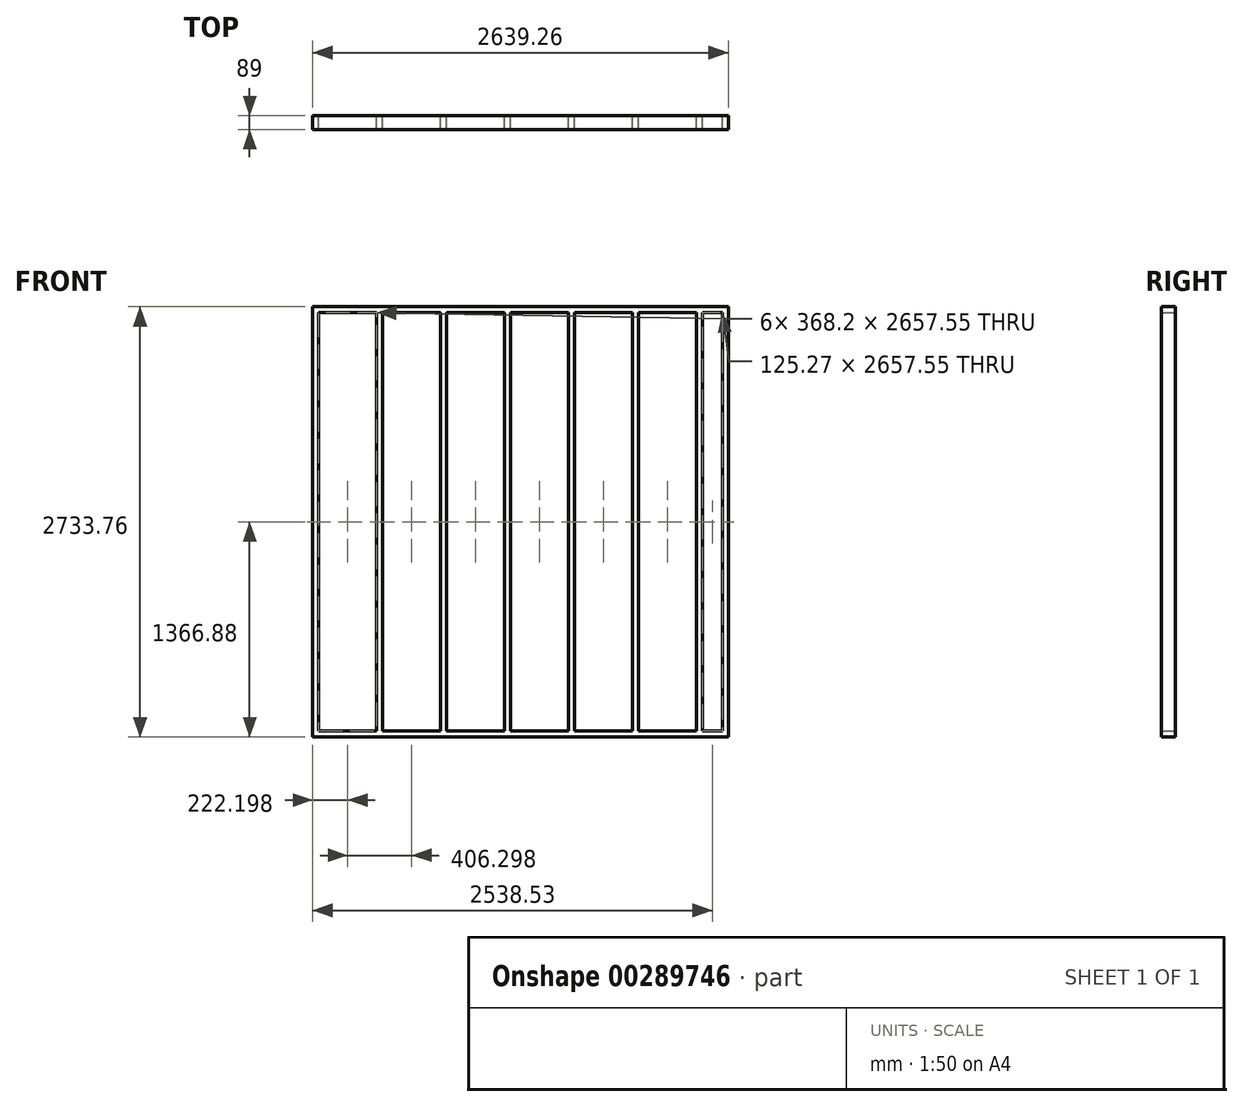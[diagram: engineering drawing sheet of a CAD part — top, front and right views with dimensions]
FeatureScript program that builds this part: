
annotation { "Feature Type Name" : "Feature", "Feature Type Description" : "" }
export const myFeature = defineFeature(function(context is Context, id is Id, definition is map)
    precondition{}
    {
        {
            var Q0;
            Q0=qCreatedBy(makeId("Front.planeOp"),FACE);
            var sketch = newSketch(context, id + "F0", { "sketchPlane" : qUnion([Q0])});
            skLineSegment(sketch, "E0.bottom", {"start": v(1319.63, -1366.88) * mm, "end": v(-1319.63, -1366.88) * mm});
            skLineSegment(sketch, "E0.top", {"start": v(1319.63, 1366.88) * mm, "end": v(-1319.63, 1366.88) * mm});
            skLineSegment(sketch, "E0.left", {"start": v(1319.63, -1366.88) * mm, "end": v(1319.63, 1366.88) * mm});
            skLineSegment(sketch, "E0.right", {"start": v(-1319.63, -1366.88) * mm, "end": v(-1319.63, 1366.88) * mm});
            skPoint(sketch, "E0.middle", {"position": v(0, 0) * mm});
            skLineSegment(sketch, "E1.bottom", {"start": v(1281.53, -1328.78) * mm, "end": v(-1281.53, -1328.78) * mm});
            skLineSegment(sketch, "E1.top", {"start": v(1281.53, 1328.78) * mm, "end": v(-1281.53, 1328.78) * mm});
            skLineSegment(sketch, "E1.left", {"start": v(1281.53, -1328.78) * mm, "end": v(1281.53, 1328.78) * mm});
            skLineSegment(sketch, "E1.right", {"start": v(-1281.53, -1328.78) * mm, "end": v(-1281.53, 1328.78) * mm});
            skLineSegment(sketch, "E2.bottom", {"start": v(-913.33, 1328.78) * mm, "end": v(-875.23, 1328.78) * mm});
            skLineSegment(sketch, "E2.top", {"start": v(-913.33, -1328.78) * mm, "end": v(-875.23, -1328.78) * mm});
            skLineSegment(sketch, "E2.left", {"start": v(-913.33, 1328.78) * mm, "end": v(-913.33, -1328.78) * mm});
            skLineSegment(sketch, "E2.right", {"start": v(-875.23, 1328.78) * mm, "end": v(-875.23, -1328.78) * mm});
            skLineSegment(sketch, "E3.bottom", {"start": v(-507.03, 1328.78) * mm, "end": v(-468.93, 1328.78) * mm});
            skLineSegment(sketch, "E3.top", {"start": v(-507.03, -1328.78) * mm, "end": v(-468.93, -1328.78) * mm});
            skLineSegment(sketch, "E3.left", {"start": v(-507.03, 1328.78) * mm, "end": v(-507.03, -1328.78) * mm});
            skLineSegment(sketch, "E3.right", {"start": v(-468.93, 1328.78) * mm, "end": v(-468.93, -1328.78) * mm});
            skLineSegment(sketch, "E4.bottom", {"start": v(-100.74, 1328.78) * mm, "end": v(-62.64, 1328.78) * mm});
            skLineSegment(sketch, "E4.top", {"start": v(-100.74, -1328.78) * mm, "end": v(-62.64, -1328.78) * mm});
            skLineSegment(sketch, "E4.left", {"start": v(-100.74, 1328.78) * mm, "end": v(-100.74, -1328.78) * mm});
            skLineSegment(sketch, "E4.right", {"start": v(-62.64, 1328.78) * mm, "end": v(-62.64, -1328.78) * mm});
            skLineSegment(sketch, "E5.bottom", {"start": v(305.56, 1328.78) * mm, "end": v(343.66, 1328.78) * mm});
            skLineSegment(sketch, "E5.top", {"start": v(305.56, -1328.78) * mm, "end": v(343.66, -1328.78) * mm});
            skLineSegment(sketch, "E5.left", {"start": v(305.56, 1328.78) * mm, "end": v(305.56, -1328.78) * mm});
            skLineSegment(sketch, "E5.right", {"start": v(343.66, 1328.78) * mm, "end": v(343.66, -1328.78) * mm});
            skLineSegment(sketch, "E6.bottom", {"start": v(711.86, 1328.78) * mm, "end": v(749.96, 1328.78) * mm});
            skLineSegment(sketch, "E6.top", {"start": v(711.86, -1328.78) * mm, "end": v(749.96, -1328.78) * mm});
            skLineSegment(sketch, "E6.left", {"start": v(711.86, 1328.78) * mm, "end": v(711.86, -1328.78) * mm});
            skLineSegment(sketch, "E6.right", {"start": v(749.96, 1328.78) * mm, "end": v(749.96, -1328.78) * mm});
            skLineSegment(sketch, "E7.bottom", {"start": v(1118.16, 1328.78) * mm, "end": v(1156.26, 1328.78) * mm});
            skLineSegment(sketch, "E7.top", {"start": v(1118.16, -1328.78) * mm, "end": v(1156.26, -1328.78) * mm});
            skLineSegment(sketch, "E7.left", {"start": v(1118.16, 1328.78) * mm, "end": v(1118.16, -1328.78) * mm});
            skLineSegment(sketch, "E7.right", {"start": v(1156.26, 1328.78) * mm, "end": v(1156.26, -1328.78) * mm});
            skSolve(sketch);
        }
        {
            var Q0;
            Q0=makeQuery(id+"F0.imprint","IMPRINT",FACE,{"disambiguationData":[TD([[makeQuery(id+"F0.imprint","IMPRINT",EDGE,{"derivedFrom":sQuery(id+"F0.wireOp",EDGE,"E0.bottom")}),-1.0]])]});
            var Q1;
            {var subQ0=sQuery(id+"F0.wireOp",EDGE,"E2.left");Q1=makeQuery(id+"F0.imprint","IMPRINT",FACE,{"disambiguationData":[TD([[makeQuery(id+"F0.imprint","IMPRINT",EDGE,{"derivedFrom":subQ0}),1.0]])]});}
            var Q2;
            {var subQ0=sQuery(id+"F0.wireOp",EDGE,"E3.left");Q2=makeQuery(id+"F0.imprint","IMPRINT",FACE,{"disambiguationData":[TD([[makeQuery(id+"F0.imprint","IMPRINT",EDGE,{"derivedFrom":subQ0}),1.0]])]});}
            var Q3;
            {var subQ0=sQuery(id+"F0.wireOp",EDGE,"E4.left");Q3=makeQuery(id+"F0.imprint","IMPRINT",FACE,{"disambiguationData":[TD([[makeQuery(id+"F0.imprint","IMPRINT",EDGE,{"derivedFrom":subQ0}),1.0]])]});}
            var Q4;
            {var subQ0=sQuery(id+"F0.wireOp",EDGE,"E5.left");Q4=makeQuery(id+"F0.imprint","IMPRINT",FACE,{"disambiguationData":[TD([[makeQuery(id+"F0.imprint","IMPRINT",EDGE,{"derivedFrom":subQ0}),1.0]])]});}
            var Q5;
            {var subQ0=sQuery(id+"F0.wireOp",EDGE,"E6.left");Q5=makeQuery(id+"F0.imprint","IMPRINT",FACE,{"disambiguationData":[TD([[makeQuery(id+"F0.imprint","IMPRINT",EDGE,{"derivedFrom":subQ0}),1.0]])]});}
            var Q6;
            {var subQ0=sQuery(id+"F0.wireOp",EDGE,"E7.left");Q6=makeQuery(id+"F0.imprint","IMPRINT",FACE,{"disambiguationData":[TD([[makeQuery(id+"F0.imprint","IMPRINT",EDGE,{"derivedFrom":subQ0}),1.0]])]});}
            extrude(context, id + "F1", {"entities" : qUnion([Q0, Q1, Q2, Q3, Q4, Q5, Q6]), "depth" : 89 * mm, "offsetDistance" : 30.48 * mm});
        }
    });
